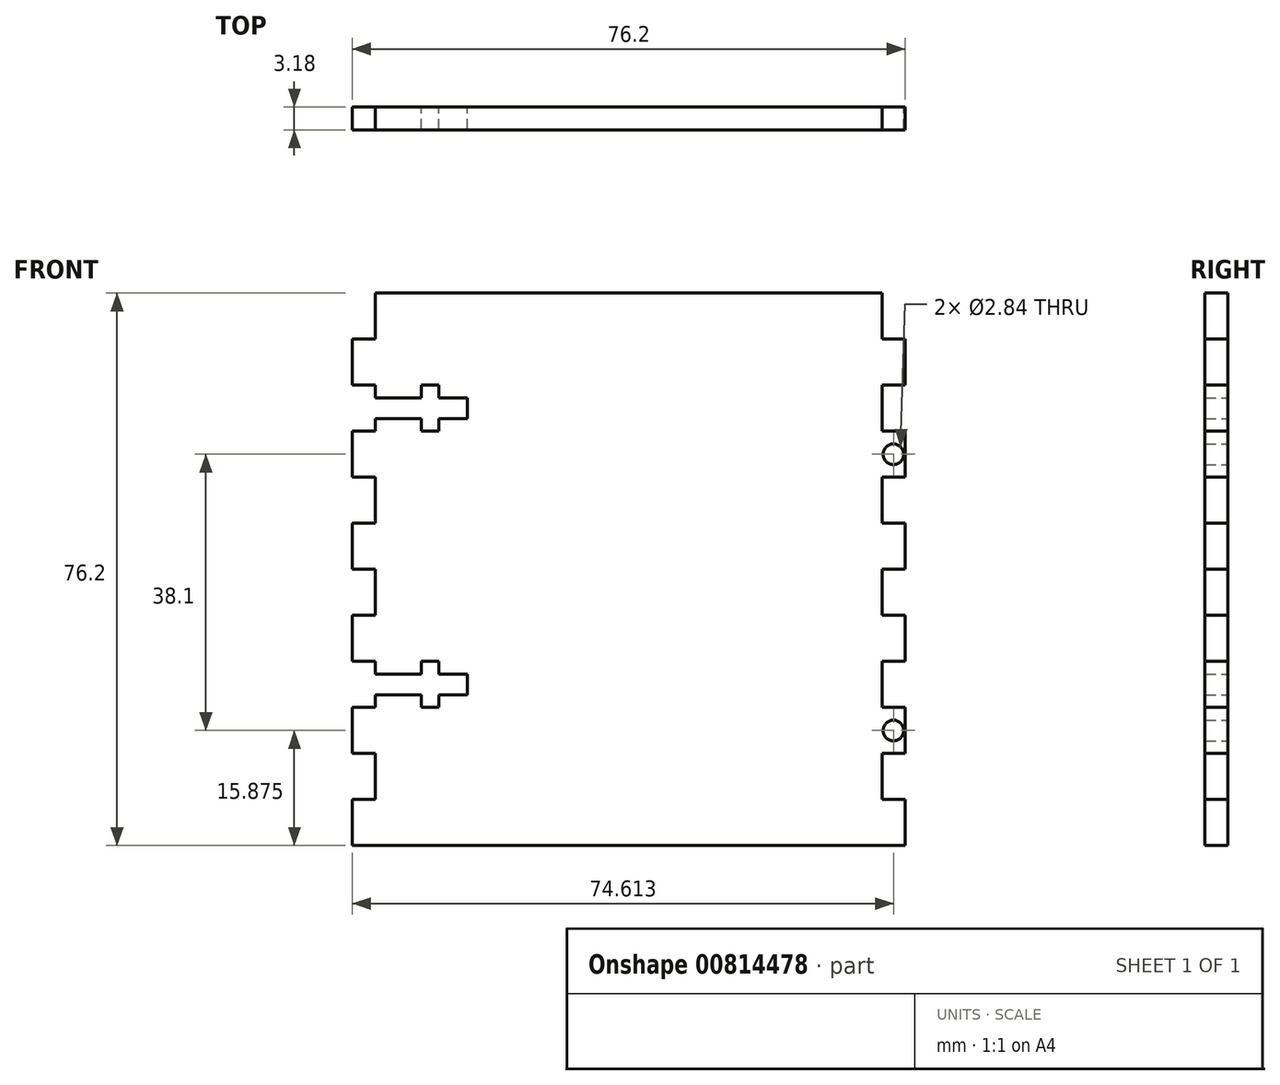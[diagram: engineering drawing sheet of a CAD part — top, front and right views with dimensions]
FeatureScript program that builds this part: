
annotation { "Feature Type Name" : "Feature", "Feature Type Description" : "" }
export const myFeature = defineFeature(function(context is Context, id is Id, definition is map)
    precondition{}
    {
        {
            var Q0;
            Q0=qCreatedBy(makeId("Front.planeOp"),FACE);
            var sketch = newSketch(context, id + "F0", { "sketchPlane" : qUnion([Q0])});
            skLineSegment(sketch, "E0.bottom", {"start": v(-38.1, 38.1) * mm, "end": v(38.1, 38.1) * mm});
            skLineSegment(sketch, "E0.top", {"start": v(-38.1, -38.1) * mm, "end": v(38.1, -38.1) * mm});
            skLineSegment(sketch, "E0.left", {"start": v(-38.1, 38.1) * mm, "end": v(-38.1, -38.1) * mm});
            skLineSegment(sketch, "E0.right", {"start": v(38.1, 38.1) * mm, "end": v(38.1, -38.1) * mm});
            skLineSegment(sketch, "E1.bottom", {"start": v(38.1, 38.1) * mm, "end": v(34.92, 38.1) * mm});
            skLineSegment(sketch, "E1.top", {"start": v(38.1, 31.75) * mm, "end": v(34.92, 31.75) * mm});
            skLineSegment(sketch, "E1.left", {"start": v(38.1, 38.1) * mm, "end": v(38.1, 31.75) * mm});
            skLineSegment(sketch, "E1.right", {"start": v(34.92, 38.1) * mm, "end": v(34.92, 31.75) * mm});
            skLineSegment(sketch, "E2.bottom", {"start": v(38.1, 25.4) * mm, "end": v(34.93, 25.4) * mm});
            skLineSegment(sketch, "E2.top", {"start": v(38.1, 19.05) * mm, "end": v(34.93, 19.05) * mm});
            skLineSegment(sketch, "E2.left", {"start": v(38.1, 25.4) * mm, "end": v(38.1, 19.05) * mm});
            skLineSegment(sketch, "E2.right", {"start": v(34.93, 25.4) * mm, "end": v(34.93, 19.05) * mm});
            skLineSegment(sketch, "E3.bottom", {"start": v(38.1, 12.7) * mm, "end": v(34.93, 12.7) * mm});
            skLineSegment(sketch, "E3.top", {"start": v(38.1, 6.35) * mm, "end": v(34.93, 6.35) * mm});
            skLineSegment(sketch, "E3.left", {"start": v(38.1, 12.7) * mm, "end": v(38.1, 6.35) * mm});
            skLineSegment(sketch, "E3.right", {"start": v(34.93, 12.7) * mm, "end": v(34.93, 6.35) * mm});
            skLineSegment(sketch, "E4.bottom", {"start": v(38.1, 0) * mm, "end": v(34.93, 0) * mm});
            skLineSegment(sketch, "E4.top", {"start": v(38.1, -6.35) * mm, "end": v(34.93, -6.35) * mm});
            skLineSegment(sketch, "E4.left", {"start": v(38.1, 0) * mm, "end": v(38.1, -6.35) * mm});
            skLineSegment(sketch, "E4.right", {"start": v(34.93, 0) * mm, "end": v(34.93, -6.35) * mm});
            skLineSegment(sketch, "E5.bottom", {"start": v(38.1, -12.7) * mm, "end": v(34.93, -12.7) * mm});
            skLineSegment(sketch, "E5.top", {"start": v(38.1, -19.05) * mm, "end": v(34.93, -19.05) * mm});
            skLineSegment(sketch, "E5.left", {"start": v(38.1, -12.7) * mm, "end": v(38.1, -19.05) * mm});
            skLineSegment(sketch, "E5.right", {"start": v(34.93, -12.7) * mm, "end": v(34.93, -19.05) * mm});
            skLineSegment(sketch, "E6.top", {"start": v(38.1, -38.1) * mm, "end": v(34.93, -38.1) * mm});
            skLineSegment(sketch, "E6.left", {"start": v(38.1, -31.75) * mm, "end": v(38.1, -38.1) * mm});
            skLineSegment(sketch, "E7.bottom", {"start": v(38.1, -25.4) * mm, "end": v(34.93, -25.4) * mm});
            skLineSegment(sketch, "E7.top", {"start": v(38.1, -31.75) * mm, "end": v(34.93, -31.75) * mm});
            skLineSegment(sketch, "E7.left", {"start": v(38.1, -25.4) * mm, "end": v(38.1, -31.75) * mm});
            skLineSegment(sketch, "E7.right", {"start": v(34.93, -25.4) * mm, "end": v(34.93, -31.75) * mm});
            skLineSegment(sketch, "E8.MirrorCS", {"start": v(-38.1, -19.05) * mm, "end": v(-34.93, -19.05) * mm});
            skLineSegment(sketch, "E9.MirrorCS", {"start": v(-38.1, 0) * mm, "end": v(-34.93, 0) * mm});
            skLineSegment(sketch, "E10.MirrorCS", {"start": v(-38.1, -6.35) * mm, "end": v(-34.93, -6.35) * mm});
            skLineSegment(sketch, "E11.MirrorCS", {"start": v(-38.1, 6.35) * mm, "end": v(-34.93, 6.35) * mm});
            skLineSegment(sketch, "E12.MirrorCS", {"start": v(-38.1, -12.7) * mm, "end": v(-34.93, -12.7) * mm});
            skLineSegment(sketch, "E13.MirrorCS", {"start": v(-38.1, -31.75) * mm, "end": v(-34.93, -31.75) * mm});
            skLineSegment(sketch, "E14.MirrorCS", {"start": v(-38.1, 12.7) * mm, "end": v(-34.93, 12.7) * mm});
            skLineSegment(sketch, "E15.MirrorCS", {"start": v(-38.1, 19.05) * mm, "end": v(-34.93, 19.05) * mm});
            skLineSegment(sketch, "E16.MirrorCS", {"start": v(-38.1, 25.4) * mm, "end": v(-34.93, 25.4) * mm});
            skLineSegment(sketch, "E17.MirrorCS", {"start": v(-38.1, 38.1) * mm, "end": v(-34.92, 38.1) * mm});
            skLineSegment(sketch, "E18.MirrorCS", {"start": v(-38.1, 31.75) * mm, "end": v(-34.92, 31.75) * mm});
            skLineSegment(sketch, "E19.MirrorCS", {"start": v(-38.1, -25.4) * mm, "end": v(-34.93, -25.4) * mm});
            skLineSegment(sketch, "E20.MirrorCS", {"start": v(-38.1, -38.1) * mm, "end": v(-34.93, -38.1) * mm});
            skLineSegment(sketch, "E21.MirrorCS", {"start": v(-34.93, -25.4) * mm, "end": v(-34.93, -31.75) * mm});
            skLineSegment(sketch, "E22.MirrorCS", {"start": v(-38.1, 12.7) * mm, "end": v(-38.1, 6.35) * mm});
            skLineSegment(sketch, "E23.MirrorCS", {"start": v(-38.1, -25.4) * mm, "end": v(-38.1, -31.75) * mm});
            skLineSegment(sketch, "E24.MirrorCS", {"start": v(-38.1, 0) * mm, "end": v(-38.1, -6.35) * mm});
            skLineSegment(sketch, "E25.MirrorCS", {"start": v(-34.93, 0) * mm, "end": v(-34.93, -6.35) * mm});
            skLineSegment(sketch, "E26.MirrorCS", {"start": v(-38.1, -12.7) * mm, "end": v(-38.1, -19.05) * mm});
            skLineSegment(sketch, "E27.MirrorCS", {"start": v(-34.93, -12.7) * mm, "end": v(-34.93, -19.05) * mm});
            skLineSegment(sketch, "E28.MirrorCS", {"start": v(-38.1, -31.75) * mm, "end": v(-38.1, -38.1) * mm});
            skLineSegment(sketch, "E29.MirrorCS", {"start": v(-34.93, 25.4) * mm, "end": v(-34.93, 19.05) * mm});
            skLineSegment(sketch, "E30.MirrorCS", {"start": v(-34.93, 12.7) * mm, "end": v(-34.93, 6.35) * mm});
            skLineSegment(sketch, "E31.MirrorCS", {"start": v(-38.1, 25.4) * mm, "end": v(-38.1, 19.05) * mm});
            skLineSegment(sketch, "E32.MirrorCS", {"start": v(-34.92, 38.1) * mm, "end": v(-34.92, 31.75) * mm});
            skLineSegment(sketch, "E33.MirrorCS", {"start": v(-38.1, 38.1) * mm, "end": v(-38.1, 31.75) * mm});
            skPoint(sketch, "E34.centerSnap0", {"position": v(34.93, 22.22) * mm});
            skCircle(sketch, "E35", {"center": v(36.51, 15.87) * mm, "radius": 1.42 * mm});
            skCircle(sketch, "E36", {"center": v(36.51, -22.23) * mm, "radius": 1.42 * mm});
            skPoint(sketch, "E36.centerSnap0", {"position": v(36.51, -12.7) * mm});
            skLineSegment(sketch, "E37.left", {"start": v(-34.92, 36.35) * mm, "end": v(-34.92, 33.5) * mm});
            skLineSegment(sketch, "E38.bottom", {"start": v(-28.57, 38.1) * mm, "end": v(-26.2, 38.1) * mm});
            skPoint(sketch, "E39.oppositeSnap0", {"position": v(-34.93, 22.22) * mm});
            skLineSegment(sketch, "E39.bottom", {"start": v(-34.93, 23.65) * mm, "end": v(-22.22, 23.65) * mm});
            skLineSegment(sketch, "E39.top", {"start": v(-34.93, 20.8) * mm, "end": v(-22.22, 20.8) * mm});
            skLineSegment(sketch, "E39.left", {"start": v(-34.93, 23.65) * mm, "end": v(-34.93, 20.8) * mm});
            skLineSegment(sketch, "E39.right", {"start": v(-22.22, 23.65) * mm, "end": v(-22.22, 20.8) * mm});
            skLineSegment(sketch, "E40.left", {"start": v(-34.93, 10.95) * mm, "end": v(-34.93, 8.1) * mm});
            skLineSegment(sketch, "E41.bottom", {"start": v(-28.58, 25.4) * mm, "end": v(-26.19, 25.4) * mm});
            skLineSegment(sketch, "E41.top", {"start": v(-28.58, 19.05) * mm, "end": v(-26.19, 19.05) * mm});
            skLineSegment(sketch, "E41.left", {"start": v(-28.58, 25.4) * mm, "end": v(-28.58, 19.05) * mm});
            skLineSegment(sketch, "E41.right", {"start": v(-26.19, 25.4) * mm, "end": v(-26.19, 19.05) * mm});
            skLineSegment(sketch, "E42.left", {"start": v(-34.93, -1.75) * mm, "end": v(-34.93, -4.6) * mm});
            skLineSegment(sketch, "E43.bottom", {"start": v(-34.93, -14.45) * mm, "end": v(-22.23, -14.45) * mm});
            skLineSegment(sketch, "E43.top", {"start": v(-34.93, -17.3) * mm, "end": v(-22.23, -17.3) * mm});
            skLineSegment(sketch, "E43.left", {"start": v(-34.93, -14.45) * mm, "end": v(-34.93, -17.3) * mm});
            skLineSegment(sketch, "E43.right", {"start": v(-22.23, -14.45) * mm, "end": v(-22.23, -17.3) * mm});
            skLineSegment(sketch, "E44.bottom", {"start": v(-28.58, -12.7) * mm, "end": v(-26.19, -12.7) * mm});
            skLineSegment(sketch, "E44.top", {"start": v(-28.58, -19.05) * mm, "end": v(-26.19, -19.05) * mm});
            skLineSegment(sketch, "E44.left", {"start": v(-28.58, -12.7) * mm, "end": v(-28.58, -19.05) * mm});
            skLineSegment(sketch, "E44.right", {"start": v(-26.19, -12.7) * mm, "end": v(-26.19, -19.05) * mm});
            skLineSegment(sketch, "E45.left", {"start": v(-34.93, -27.15) * mm, "end": v(-34.93, -30) * mm});
            skSolve(sketch);
        }
        {
            var Q0;
            Q0=makeQuery(id+"F0.imprint","IMPRINT",FACE,{"disambiguationData":[TD([[makeQuery(id+"F0.imprint","IMPRINT",EDGE,{"derivedFrom":sQuery(id+"F0.wireOp",EDGE,"E0.bottom")}),-1.0]])]});
            var Q1;
            Q1=makeQuery(id+"F0.imprint","IMPRINT",FACE,{"disambiguationData":[TD([[makeQuery(id+"F0.imprint","IMPRINT",EDGE,{"derivedFrom":sQuery(id+"F0.wireOp",EDGE,"E0.top")}),1.0]])]});
            extrude(context, id + "F1", {"entities" : qUnion([Q0, Q1]), "depth" : 3.17 * mm, "offsetDistance" : 25.4 * mm});
        }
    });
